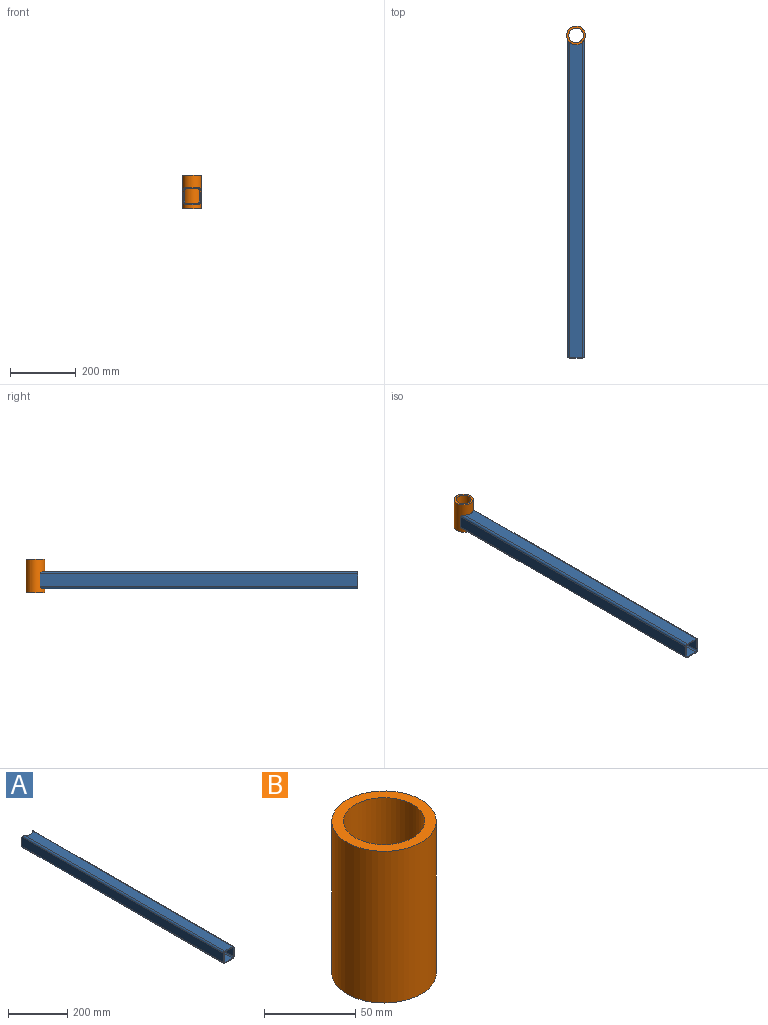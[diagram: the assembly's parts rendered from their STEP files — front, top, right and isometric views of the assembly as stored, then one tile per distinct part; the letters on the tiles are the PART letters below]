
ASSEMBLY  parts=2 mates=1
PART A: 18 faces, bbox 50.8x965.2x50.8 mm
  f0: plane 956.99x38.1mm, normal (0,0,1), area 36271.3mm2, adj f3,f4,f16,f17
  f1: plane 956.99x38.1mm, normal (0,0,-1), area 36271.3mm2, adj f6,f15,f16,f17
  f2: plane 965.2x38.1mm, normal (1,0,0), area 36774.1mm2, adj f3,f15,f16,f17
  f3: cylinder r=6.35mm len=965.2mm, axis (0,1,0), area 9593.3mm2, adj f0,f2,f16,f17
  f4: cylinder r=6.35mm len=965.2mm, axis (0,1,0), area 9593.3mm2, adj f0,f5,f16,f17
  f5: plane 965.2x38.1mm, normal (-1,0,0), area 36774.1mm2, adj f4,f6,f16,f17
  f6: cylinder r=6.35mm len=965.2mm, axis (0,1,0), area 9593.3mm2, adj f1,f5,f16,f17
  f7: cylinder r=4.57mm len=960.33mm, axis (0,1,0), area 6884mm2, adj f8,f14,f16,f17
  f8: plane 955.82x35.31mm, normal (0,0,-1), area 33599.1mm2, adj f7,f9,f16,f17
  f9: cylinder r=4.57mm len=960.33mm, axis (0,1,0), area 6884mm2, adj f8,f10,f16,f17
  f10: plane 960.33x35.31mm, normal (-1,0,0), area 33905.4mm2, adj f9,f11,f16,f17
  f11: cylinder r=4.57mm len=960.33mm, axis (0,1,0), area 6884mm2, adj f10,f12,f16,f17
  f12: plane 955.82x35.31mm, normal (0,0,1), area 33599.1mm2, adj f11,f13,f16,f17
  f13: cylinder r=4.57mm len=960.33mm, axis (0,1,0), area 6884mm2, adj f12,f14,f16,f17
  f14: plane 960.33x35.31mm, normal (1,0,0), area 33905.4mm2, adj f7,f13,f16,f17
  f15: cylinder r=6.35mm len=965.2mm, axis (0,1,0), area 9593.3mm2, adj f1,f2,f16,f17
  f16: plane 50.8x50.8mm, normal (0,-1,0), area 588.2mm2, adj f0,f1,f2,f3,f4,f5,f6,f7
  f17: cylinder r=28.57mm len=50.8mm, axis (0,0,1), area 876.9mm2, adj f0,f1,f2,f3,f4,f5,f6,f7
PART B: 4 faces, bbox 57.2x57.2x101.6 mm
  f0: cylinder r=22.23mm len=101.6mm, axis (0,0,-1), area 14187.8mm2, adj f2,f3
  f1: cylinder r=28.57mm len=101.6mm, axis (0,0,-1), area 18241.5mm2, adj f2,f3
  f2: plane 57.15x57.15mm, normal (0,0,1), area 1013.4mm2, adj f0,f1
  f3: plane 57.15x57.15mm, normal (0,0,-1), area 1013.4mm2, adj f0,f1
PLACE A t=(-76.78,439.81,84.36)mm
PLACE B t=(-76.78,452.9,46.26)mm
MATE fastened B.f1 <-> A.f17  axis (0,0,-1) through (-76.78,452.9,97.06)mm
